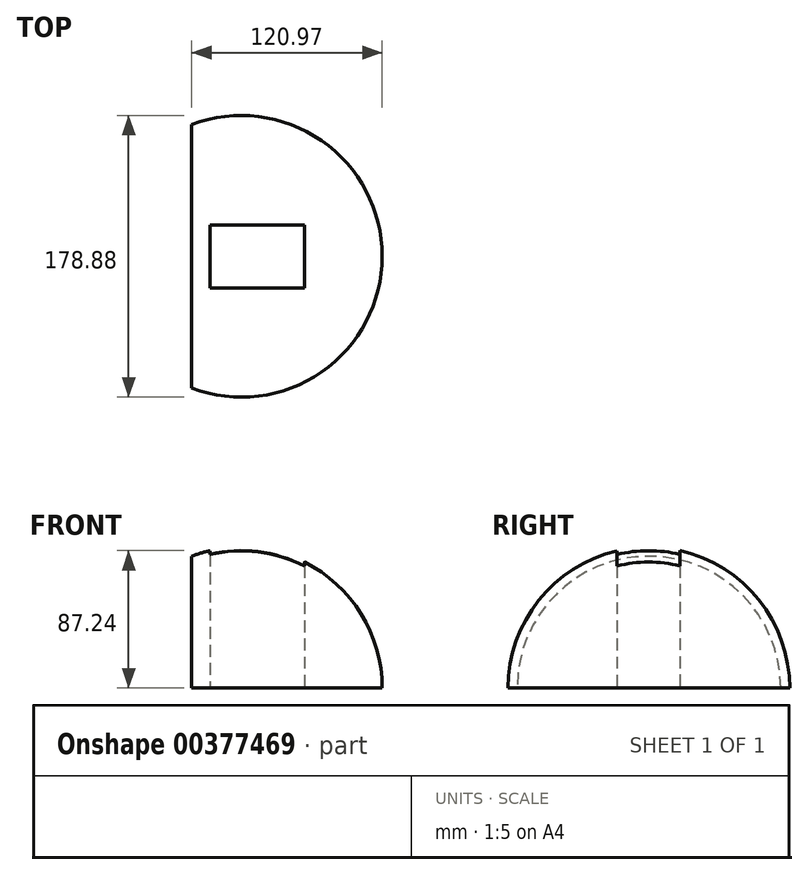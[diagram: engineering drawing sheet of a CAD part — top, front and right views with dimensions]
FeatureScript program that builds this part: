
annotation { "Feature Type Name" : "Feature", "Feature Type Description" : "" }
export const myFeature = defineFeature(function(context is Context, id is Id, definition is map)
    precondition{}
    {
        {
            var Q0;
            Q0=qCreatedBy(makeId("Top.planeOp"),FACE);
            var sketch = newSketch(context, id + "F0", { "sketchPlane" : qUnion([Q0])});
            skLineSegment(sketch, "E0.bottom", {"start": v(-20, 19.75) * mm, "end": v(40, 19.75) * mm});
            skLineSegment(sketch, "E0.top", {"start": v(-20, -20.25) * mm, "end": v(40, -20.25) * mm});
            skLineSegment(sketch, "E0.left", {"start": v(-20, 19.75) * mm, "end": v(-20, -20.25) * mm});
            skLineSegment(sketch, "E0.right", {"start": v(40, 19.75) * mm, "end": v(40, -20.25) * mm});
            skSolve(sketch);
        }
        {
            var Q0;
            Q0=makeQuery(id+"F0.imprint","IMPRINT",FACE,{"disambiguationData":[TD([[makeQuery(id+"F0.imprint","IMPRINT",EDGE,{"derivedFrom":sQuery(id+"F0.wireOp",EDGE,"E0.bottom")}),-1.0]])]});
            var Q1;
            Q1 = qSketchRegion(id + "F0", true);
            extrude(context, id + "F1", {"entities" : qUnion([Q0, Q1]), "depth" : 80 * mm});
        }
        {
            var Q0;
            Q0=qCreatedBy(makeId("Front.planeOp"),FACE);
            var sketch = newSketch(context, id + "F2", { "sketchPlane" : qUnion([Q0])});
            skLineSegment(sketch, "E1.0", {"start": v(-20, 80) * mm, "end": v(40, 80) * mm});
            skLineSegment(sketch, "E2.1", {"start": v(40, 80) * mm, "end": v(40, 0) * mm});
            skArc(sketch, "E3", {"start": v(89.44, 0) * mm, "mid": v(0, 89.44) * mm, "end": v(-89.44, 0) * mm});
            skLineSegment(sketch, "E4", {"start": v(-89.44, 0) * mm, "end": v(89.44, 0) * mm});
            skPoint(sketch, "E5.orphan", {"position": v(-60.3, 0) * mm});
            skSolve(sketch);
        }
        {
            var Q0;
            {var subQ0=sQuery(id+"F2.wireOp",EDGE,"E2.1");Q0=makeQuery(id+"F2.imprint","IMPRINT",FACE,{"disambiguationData":[TD([[makeQuery(id+"F2.imprint","IMPRINT",EDGE,{"derivedFrom":subQ0}),1.0]])]});}
            var Q1;
            {var subQ0=sQuery(id+"F2.wireOp",EDGE,"E2.1");Q1=makeQuery(id+"F2.imprint","IMPRINT",FACE,{"disambiguationData":[TD([[makeQuery(id+"F2.imprint","IMPRINT",EDGE,{"derivedFrom":subQ0}),-1.0]])]});}
            var Q2;
            Q2=sQuery(id+"F2.wireOp",EDGE,"E4");
            revolve(context, id + "F3", {"operationType" : NewBodyOperationType.ADD, "entities" : qUnion([Q0, Q1]), "axis" : qUnion([Q2]), "revolveType" : RevolveType.FULL});
        }
        {
            var Q0;
            Q0=makeQuery(id+"F1.opExtrude","CAP_FACE",FACE,{"disambiguationData":[OSD([sQuery(id+"F0.wireOp",EDGE,"E0.bottom"),sQuery(id+"F0.wireOp",EDGE,"E0.top"),sQuery(id+"F0.wireOp",EDGE,"E0.left"),sQuery(id+"F0.wireOp",EDGE,"E0.right")])],"isStart":false});
            var sketch = newSketch(context, id + "F4", { "sketchPlane" : qUnion([Q0])});
            skLineSegment(sketch, "E6.bottom", {"start": v(40, -20.25) * mm, "end": v(-20, -20.25) * mm});
            skLineSegment(sketch, "E6.top", {"start": v(40, 19.75) * mm, "end": v(-20, 19.75) * mm});
            skLineSegment(sketch, "E6.left", {"start": v(40, -20.25) * mm, "end": v(40, 19.75) * mm});
            skLineSegment(sketch, "E6.right", {"start": v(-20, -20.25) * mm, "end": v(-20, 19.75) * mm});
            skSolve(sketch);
        }
        {
            var Q0;
            Q0 = qSketchRegion(id + "F4", true);
            extrude(context, id + "F5", {"entities" : qUnion([Q0]), "operationType" : NewBodyOperationType.REMOVE, "depth" : 25 * mm, "hasSecondDirection" : true, "secondDirectionOppositeDirection" : true, "secondDirectionDepth" : 80 * mm});
        }
        {
            var Q0;
            Q0=qCreatedBy(makeId("Front.planeOp"),FACE);
            var sketch = newSketch(context, id + "F6", { "sketchPlane" : qUnion([Q0])});
            skLineSegment(sketch, "E7", {"start": v(-31.53, 105.66) * mm, "end": v(-31.53, -86.37) * mm});
            skSolve(sketch);
        }
        {
            var Q0;
            Q0=sQuery(id+"F6.wireOp",EDGE,"E7");
            extrude(context, id + "F7", {"bodyType" : ToolBodyType.SURFACE, "surfaceEntities" : qUnion([Q0]), "endBound" : BoundingType.SYMMETRIC, "depth" : 176.27 * mm});
        }
        {
            var Q0;
            Q0=makeQuery(id+"F7.opExtrude","SWEPT_FACE",FACE,{"disambiguationData":[OSD([sQuery(id+"F6.wireOp",EDGE,"E7")])]});
            extrude(context, id + "F8", {"entities" : qUnion([Q0]), "operationType" : NewBodyOperationType.REMOVE, "depth" : 68.62 * mm});
        }
        {
            var Q0;
            Q0=qCreatedBy(makeId("Top.planeOp"),FACE);
            var sketch = newSketch(context, id + "F9", { "sketchPlane" : qUnion([Q0])});
            skLineSegment(sketch, "E8.bottom", {"start": v(-46.93, 116.44) * mm, "end": v(99.9, 116.44) * mm});
            skLineSegment(sketch, "E8.top", {"start": v(-46.93, -111.3) * mm, "end": v(99.9, -111.3) * mm});
            skLineSegment(sketch, "E8.left", {"start": v(-46.93, 116.44) * mm, "end": v(-46.93, -111.3) * mm});
            skLineSegment(sketch, "E8.right", {"start": v(99.9, 116.44) * mm, "end": v(99.9, -111.3) * mm});
            skSolve(sketch);
        }
        {
            var Q0;
            Q0=makeQuery(id+"F9.imprint","IMPRINT",FACE,{"disambiguationData":[TD([[makeQuery(id+"F9.imprint","IMPRINT",EDGE,{"derivedFrom":sQuery(id+"F9.wireOp",EDGE,"E8.bottom")}),-1.0]])]});
            extrude(context, id + "F10", {"entities" : qUnion([Q0]), "operationType" : NewBodyOperationType.REMOVE, "oppositeDirection" : true, "depth" : 104.34 * mm});
        }
    });
